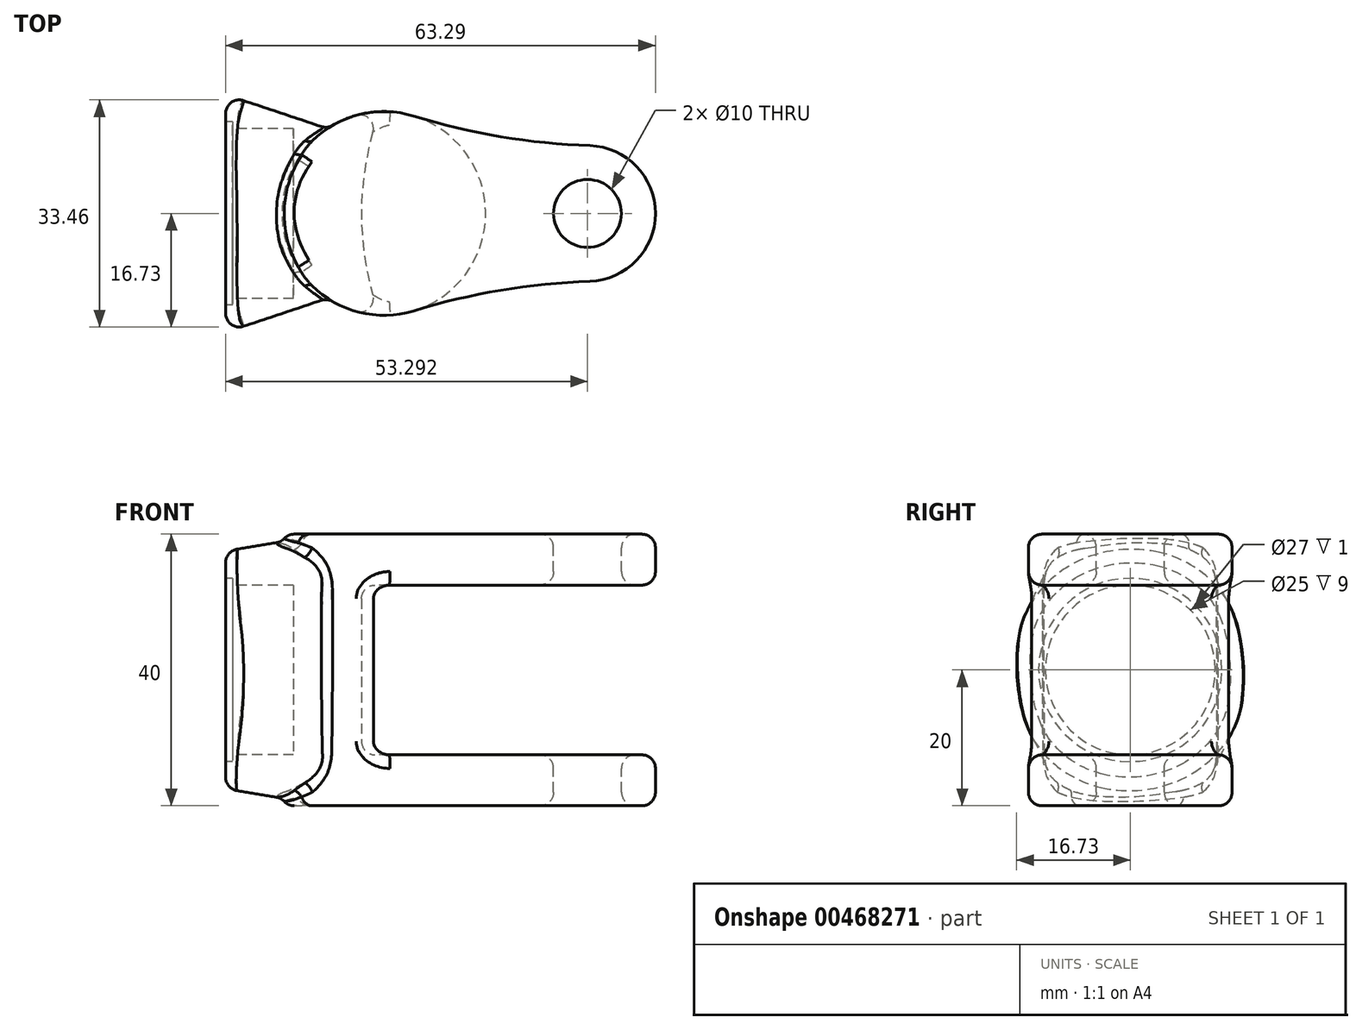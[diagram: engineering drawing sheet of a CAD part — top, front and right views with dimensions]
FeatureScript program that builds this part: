
annotation { "Feature Type Name" : "Feature", "Feature Type Description" : "" }
export const myFeature = defineFeature(function(context is Context, id is Id, definition is map)
    precondition{}
    {
        {
            var Q0;
            Q0=qCreatedBy(makeId("Right.planeOp"),FACE);
            var sketch = newSketch(context, id + "F0", { "sketchPlane" : qUnion([Q0])});
            skCircle(sketch, "E0", {"center": v(0, 0) * mm, "radius": 17.5 * mm});
            skSolve(sketch);
        }
        {
            var Q0;
            Q0=makeQuery(id+"F0.imprint","IMPRINT",FACE,{"disambiguationData":[TD([[makeQuery(id+"F0.imprint","IMPRINT",EDGE,{"derivedFrom":sQuery(id+"F0.wireOp",EDGE,"E0")}),1.0]])]});
            cPlane(context, id + "F1", {"entities" : qUnion([Q0]), "cplaneType" : CPlaneType.OFFSET, "offset" : 15 * mm, "width" : 150 * mm, "height" : 150 * mm});
        }
        {
            var Q0;
            Q0=qCreatedBy(id+"F1.planeOp",FACE);
            var sketch = newSketch(context, id + "F2", { "sketchPlane" : qUnion([Q0])});
            skLineSegment(sketch, "E1.bottom", {"start": v(-5, -20) * mm, "end": v(5, -20) * mm});
            skLineSegment(sketch, "E1.top", {"start": v(-5, 20) * mm, "end": v(5, 20) * mm});
            skLineSegment(sketch, "E1.left", {"start": v(-12.5, -12.5) * mm, "end": v(-12.5, 12.5) * mm});
            skLineSegment(sketch, "E1.right", {"start": v(12.5, -12.5) * mm, "end": v(12.5, 12.5) * mm});
            skPoint(sketch, "E1.middle", {"position": v(0, 0) * mm});
            skPoint(sketch, "E2.visualSharp", {"position": v(-12.5, -20) * mm});
            skArc(sketch, "E2.filletArc", {"start": v(-12.5, -12.5) * mm, "mid": v(-10.3, -17.8) * mm, "end": v(-5, -20) * mm});
            skPoint(sketch, "E3.visualSharp", {"position": v(12.5, -20) * mm});
            skArc(sketch, "E3.filletArc", {"start": v(5, -20) * mm, "mid": v(10.3, -17.8) * mm, "end": v(12.5, -12.5) * mm});
            skPoint(sketch, "E4.visualSharp", {"position": v(-12.5, 20) * mm});
            skArc(sketch, "E4.filletArc", {"start": v(-5, 20) * mm, "mid": v(-10.3, 17.8) * mm, "end": v(-12.5, 12.5) * mm});
            skPoint(sketch, "E5.visualSharp", {"position": v(12.5, 20) * mm});
            skArc(sketch, "E5.filletArc", {"start": v(12.5, 12.5) * mm, "mid": v(10.3, 17.8) * mm, "end": v(5, 20) * mm});
            skSolve(sketch);
        }
        {
            var Q0;
            Q0=makeQuery(id+"F0.imprint","IMPRINT",FACE,{"disambiguationData":[TD([[makeQuery(id+"F0.imprint","IMPRINT",EDGE,{"derivedFrom":sQuery(id+"F0.wireOp",EDGE,"E0")}),1.0]])]});
            var Q1;
            Q1=makeQuery(id+"F2.imprint","IMPRINT",FACE,{"disambiguationData":[TD([[makeQuery(id+"F2.imprint","IMPRINT",EDGE,{"derivedFrom":sQuery(id+"F2.wireOp",EDGE,"E1.bottom")}),1.0]])]});
            loft(context, id + "F3", {"sheetProfilesArray" : [{ "sheetProfileEntities" : qUnion([Q0]) }, { "sheetProfileEntities" : qUnion([Q1]) }]});
        }
        {
            var Q0;
            Q0=qCreatedBy(makeId("Top.planeOp"),FACE);
            var sketch = newSketch(context, id + "F4", { "sketchPlane" : qUnion([Q0])});
            skArc(sketch, "E6", {"start": v(27.7, 14.34) * mm, "mid": v(8.3, 0) * mm, "end": v(27.7, -14.34) * mm});
            skArc(sketch, "E7", {"start": v(53.63, -10) * mm, "mid": v(63.3, 0) * mm, "end": v(53.63, 10) * mm});
            skLineSegment(sketch, "E8", {"start": v(23.3, 0) * mm, "end": v(53.3, 0) * mm, "construction": true});
            skArc(sketch, "E9", {"start": v(27.7, 14.34) * mm, "mid": v(40.52, 11.31) * mm, "end": v(53.63, 10) * mm});
            skArc(sketch, "E10.MirrorCS", {"start": v(27.7, -14.34) * mm, "mid": v(40.52, -11.31) * mm, "end": v(53.63, -10) * mm});
            skSolve(sketch);
        }
        {
            var Q0;
            Q0=qSketchRegion(id+"F4",true);
            extrude(context, id + "F5", {"entities" : qUnion([Q0]), "operationType" : NewBodyOperationType.ADD, "endBound" : BoundingType.SYMMETRIC, "depth" : 40 * mm});
        }
        {
            var Q0;
            Q0=qCreatedBy(makeId("Front.planeOp"),FACE);
            var sketch = newSketch(context, id + "F6", { "sketchPlane" : qUnion([Q0])});
            skLineSegment(sketch, "E11.bottom", {"start": v(20, 12.5) * mm, "end": v(63.3, 12.5) * mm});
            skLineSegment(sketch, "E11.top", {"start": v(20, -12.5) * mm, "end": v(63.3, -12.5) * mm});
            skLineSegment(sketch, "E11.left", {"start": v(20, 12.5) * mm, "end": v(20, -12.5) * mm});
            skLineSegment(sketch, "E11.right", {"start": v(63.3, 12.5) * mm, "end": v(63.3, -12.5) * mm});
            skSolve(sketch);
        }
        {
            var Q0;
            Q0=qSketchRegion(id+"F6",true);
            var Q1;
            Q1=sQuery(id+"F6.wireOp",EDGE,"E11.right");
            revolve(context, id + "F7", {"operationType" : NewBodyOperationType.REMOVE, "entities" : qUnion([Q0]), "axis" : qUnion([Q1]), "revolveType" : RevolveType.FULL, "oppositeDirection" : true});
        }
        {
            var Q0;
            Q0=makeQuery(id+"F3.opLoft","CAP_FACE",FACE,{"disambiguationData":[OSD([makeQuery(id+"F0.imprint","IMPRINT",FACE,{"disambiguationData":[TD([[makeQuery(id+"F0.imprint","IMPRINT",EDGE,{"derivedFrom":sQuery(id+"F0.wireOp",EDGE,"E0")}),1.0]])]})])],"isStart":true});
            var sketch = newSketch(context, id + "F8", { "sketchPlane" : qUnion([Q0])});
            skCircle(sketch, "E12", {"center": v(0, 0) * mm, "radius": 12.5 * mm});
            skSolve(sketch);
        }
        {
            var Q0;
            Q0=qSketchRegion(id+"F8",true);
            extrude(context, id + "F9", {"entities" : qUnion([Q0]), "operationType" : NewBodyOperationType.REMOVE, "oppositeDirection" : true, "depth" : 10 * mm});
        }
        {
            var Q0;
            Q0=makeQuery(id+"F3.opLoft","CAP_FACE",FACE,{"disambiguationData":[OSD([makeQuery(id+"F0.imprint","IMPRINT",FACE,{"disambiguationData":[TD([[makeQuery(id+"F0.imprint","IMPRINT",EDGE,{"derivedFrom":sQuery(id+"F0.wireOp",EDGE,"E0")}),1.0]])]})])],"isStart":true});
            var sketch = newSketch(context, id + "F10", { "sketchPlane" : qUnion([Q0])});
            skCircle(sketch, "E13.0", {"center": v(0, 0) * mm, "radius": 13.5 * mm});
            skSolve(sketch);
        }
        {
            var Q0;
            Q0=qSketchRegion(id+"F10",true);
            extrude(context, id + "F11", {"entities" : qUnion([Q0]), "operationType" : NewBodyOperationType.REMOVE, "oppositeDirection" : true, "depth" : 1 * mm});
        }
        {
            var Q0;
            Q0=makeQuery(id+"F5.opExtrude","CAP_FACE",FACE,{"disambiguationData":[OSD([sQuery(id+"F4.wireOp",EDGE,"E6"),sQuery(id+"F4.wireOp",EDGE,"E7"),sQuery(id+"F4.wireOp",EDGE,"E9"),sQuery(id+"F4.wireOp",EDGE,"E10.MirrorCS")])],"isStart":false});
            var sketch = newSketch(context, id + "F12", { "sketchPlane" : qUnion([Q0])});
            skCircle(sketch, "E14", {"center": v(53.3, 0) * mm, "radius": 5 * mm});
            skSolve(sketch);
        }
        {
            var Q0;
            Q0=makeQuery(id+"F12.imprint","IMPRINT",FACE,{"disambiguationData":[TD([[makeQuery(id+"F12.imprint","IMPRINT",EDGE,{"derivedFrom":sQuery(id+"F12.wireOp",EDGE,"E14")}),1.0]])]});
            extrude(context, id + "F13", {"entities" : qUnion([Q0]), "operationType" : NewBodyOperationType.REMOVE, "endBound" : BoundingType.THROUGH_ALL, "oppositeDirection" : true, "depth" : 25 * mm});
        }
        {
            var Q0;
            Q0=makeQuery(id+"F5.opExtrude","CAP_FACE",FACE,{"disambiguationData":[OSD([sQuery(id+"F4.wireOp",EDGE,"E6"),sQuery(id+"F4.wireOp",EDGE,"E7"),sQuery(id+"F4.wireOp",EDGE,"E9"),sQuery(id+"F4.wireOp",EDGE,"E10.MirrorCS")])],"isStart":false});
            var Q1;
            Q1=makeQuery(id+"F5.opExtrude","CAP_FACE",FACE,{"disambiguationData":[OSD([sQuery(id+"F4.wireOp",EDGE,"E6"),sQuery(id+"F4.wireOp",EDGE,"E7"),sQuery(id+"F4.wireOp",EDGE,"E9"),sQuery(id+"F4.wireOp",EDGE,"E10.MirrorCS")])],"isStart":true});
            var Q2;
            Q2=makeQuery(id+"F7.boolean.opBoolean","COPY",EDGE,{"derivedFrom":makeQuery(id+"F7.opRevolve","SWEPT_EDGE",EDGE,{"disambiguationData":[OSD([sQuery(id+"F6.wireOp",EDGE,"E11.bottom"),sQuery(id+"F6.wireOp",EDGE,"E11.left")])]})});
            var Q3;
            Q3=makeQuery(id+"F7.boolean.opBoolean","COPY",EDGE,{"derivedFrom":makeQuery(id+"F7.opRevolve","SWEPT_EDGE",EDGE,{"disambiguationData":[OSD([sQuery(id+"F6.wireOp",EDGE,"E11.top"),sQuery(id+"F6.wireOp",EDGE,"E11.left")])]})});
            fillet(context, id + "F14", {"entities" : qUnion([Q0, Q1, Q2, Q3]), "radius" : 2 * mm, "tangentPropagation" : true, "allowEdgeOverflow" : false});
        }
        {
            var Q0;
            Q0=makeQuery(id+"F7.boolean.opBoolean","COPY",FACE,{"derivedFrom":makeQuery(id+"F7.opRevolve","SWEPT_FACE",FACE,{"disambiguationData":[OSD([sQuery(id+"F6.wireOp",EDGE,"E11.top")])]})});
            var Q1;
            Q1=makeQuery(id+"F7.boolean.opBoolean","COPY",FACE,{"derivedFrom":makeQuery(id+"F7.opRevolve","SWEPT_FACE",FACE,{"disambiguationData":[OSD([sQuery(id+"F6.wireOp",EDGE,"E11.bottom")])]})});
            fillet(context, id + "F15", {"entities" : qUnion([Q0, Q1]), "radius" : 2 * mm, "tangentPropagation" : true, "allowEdgeOverflow" : false});
        }
        {
            var Q0;
            Q0=makeQuery(id+"F3.opLoft","MID_CAP_EDGE",EDGE,{"disambiguationData":[OSD([sQuery(id+"F2.wireOp",EDGE,"E1.right"),sQuery(id+"F2.wireOp",EDGE,"E3.filletArc"),sQuery(id+"F2.wireOp",EDGE,"E5.filletArc")])],"capPos":1.0});
            var Q1;
            Q1=makeQuery(id+"F5.boolean.opBoolean","INTERSECT",EDGE,{"disambiguationData":[OD(1.0)],"derivedFrom":[makeQuery(id+"F3.opLoft","SWEPT_FACE",FACE,{"disambiguationData":[OSD([sQuery(id+"F0.wireOp",EDGE,"E0"),sQuery(id+"F2.wireOp",EDGE,"E1.bottom"),sQuery(id+"F2.wireOp",EDGE,"E2.filletArc"),sQuery(id+"F2.wireOp",EDGE,"E3.filletArc")])]}),makeQuery(id+"F5.opExtrude","SWEPT_FACE",FACE,{"disambiguationData":[OSD([sQuery(id+"F4.wireOp",EDGE,"E6")])]})]});
            var Q2;
            Q2=makeQuery(id+"F3.opLoft","SWEPT_FACE",FACE,{"disambiguationData":[OSD([sQuery(id+"F0.wireOp",EDGE,"E0"),sQuery(id+"F2.wireOp",EDGE,"E1.bottom"),sQuery(id+"F2.wireOp",EDGE,"E2.filletArc"),sQuery(id+"F2.wireOp",EDGE,"E3.filletArc")])]});
            fillet(context, id + "F16", {"entities" : qUnion([Q0, Q1, Q2]), "radius" : 2 * mm, "tangentPropagation" : true, "allowEdgeOverflow" : false});
        }
    });
